# Revit family: Gira_257200
name_source: partatom
category: Electrical Fixtures
revit_build: Autodesk Revit 2017 (Build: 20160225_1515(x64)
units: mm (PartAtom-declared; Revit-internal decimal feet)

## family parameters
Cut with Voids When Loaded = No
Host = Face
Maintain Annotation Orientation = No
Part Type = Normal
Room Calculation Point = No
Round Connector Dimension = Use Diameter
Shared = No

## types (1)
- DCS-Repeater DRA Door communication
    App control via Bluetooth = No
    Applicable with button = No
    Applicable with infrared button = No
    Applicable with movement sensor = No
    Applicable with presence indicator = No
    Applicable with time switch/timer = No
    Applicable with transmission button = No
    BIM = https://media.live.bim.site X1 REG KNX.rfa
    BIMSITE_PRODUCT_ID = 52df534c91ab5ae52374698e5abb2b8be813e452
    Bus connection included = No
    Cost = 0 $
    Default Elevation = 1219 mm
    Description = DCS repeater Door DCS repeater,DRA Features: - Active component for extending a Gira door communication system with audio and video function. - Range extension and increase of the number of devices when using additional control devices. - Amplification of the audio and data signals of the door communication system in both directions. Repeater mode: - Interconnects two line segments, to double both the number of devices in a video or audio door communication system and the cable range. - Important: An additional control device is required to supply power to the second line segment. Multi-conversation mode: - In multi-conversation mode, the complete system is subdivided into several lines (one main line, up to five ancillary lines) interconnected via the DCS repeater. - Power is supplied to each line by its own control device. - Up to five DCS repeaters can be used in one system in multi-conversation mode.,Notes : - Data backup   The configuration of the DCS repeater can be backed up to a microSD card. - Commissioning   The DCS repeater can also be commissioned without a microSD card.
    Dimming phase cut-off = No
    Dimming phase cut-on = No
    GTIN = 4010337011125
    HAN = 257200
    Halogen free = No
    HeinzeBIM = https://www.heinze.de
    Light value memory = No
    Manufacturer = Gira
    Number of inputs = 0
    Radio frequent bidirectional = No
    Serial dimmer = No
    Transparent = No
    URL = https://www.gira.de
    With label area = No

## geometry (parser evidence)
native form markers: Blend x2, Sweep x3
no freeform markers — native parametric forms only
